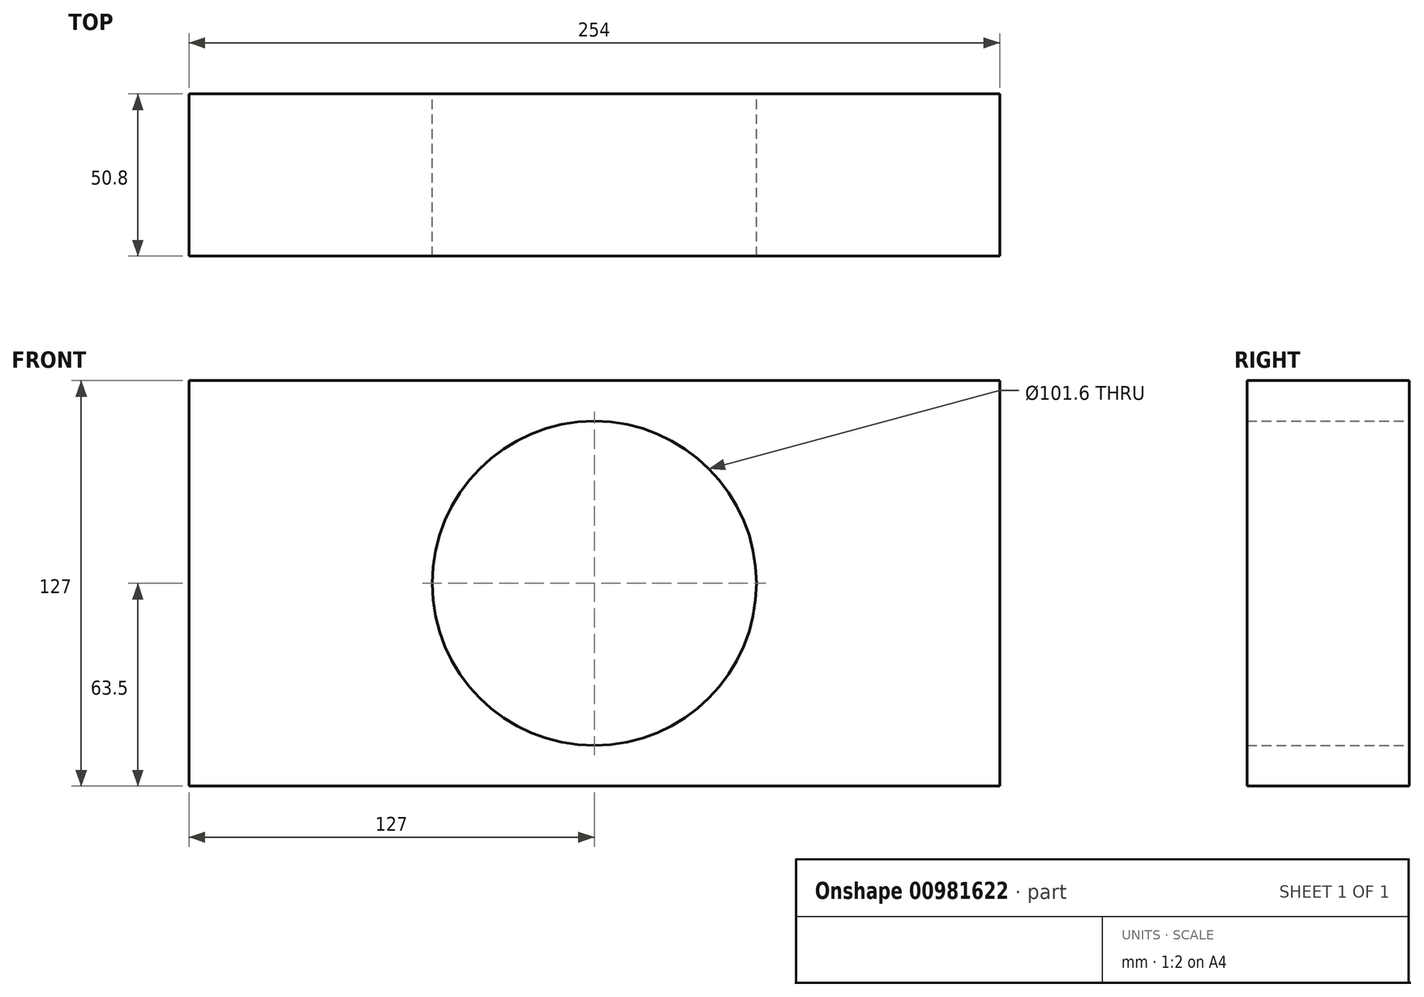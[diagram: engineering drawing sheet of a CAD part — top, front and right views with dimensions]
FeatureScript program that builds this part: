
annotation { "Feature Type Name" : "Feature", "Feature Type Description" : "" }
export const myFeature = defineFeature(function(context is Context, id is Id, definition is map)
    precondition{}
    {
        {
            var Q0;
            Q0=qCreatedBy(makeId("Front.planeOp"),FACE);
            var sketch = newSketch(context, id + "F0", { "sketchPlane" : qUnion([Q0])});
            skLineSegment(sketch, "E0.bottom", {"start": v(-127, -63.5) * mm, "end": v(127, -63.5) * mm});
            skLineSegment(sketch, "E0.top", {"start": v(-127, 63.5) * mm, "end": v(127, 63.5) * mm});
            skLineSegment(sketch, "E0.left", {"start": v(-127, -63.5) * mm, "end": v(-127, 63.5) * mm});
            skLineSegment(sketch, "E0.right", {"start": v(127, -63.5) * mm, "end": v(127, 63.5) * mm});
            skPoint(sketch, "E0.middle", {"position": v(0, 0) * mm});
            skCircle(sketch, "E1", {"center": v(0, 0) * mm, "radius": 50.8 * mm});
            skSolve(sketch);
        }
        {
            var Q0;
            Q0=makeQuery(id+"F0.imprint","IMPRINT",FACE,{"disambiguationData":[TD([[makeQuery(id+"F0.imprint","IMPRINT",EDGE,{"derivedFrom":sQuery(id+"F0.wireOp",EDGE,"E0.bottom")}),1.0]])]});
            var Q1;
            Q1 = qSketchRegion(id + "F2", true);
            extrude(context, id + "F1", {"entities" : qUnion([Q0, Q1]), "depth" : 50.8 * mm, "offsetDistance" : 25 * mm});
        }
        {
            var Q0;
            Q0=makeQuery(id+"F1.opExtrude","CAP_FACE",FACE,{"disambiguationData":[OSD([sQuery(id+"F0.wireOp",EDGE,"E0.bottom"),sQuery(id+"F0.wireOp",EDGE,"E0.top"),sQuery(id+"F0.wireOp",EDGE,"E0.left"),sQuery(id+"F0.wireOp",EDGE,"E0.right"),sQuery(id+"F0.wireOp",EDGE,"E1")])],"isStart":false});
            var sketch = newSketch(context, id + "F2", { "sketchPlane" : qUnion([Q0])});
            skLineSegment(sketch, "E2.bottom", {"start": v(-105.35, 63.5) * mm, "end": v(-79.95, 63.5) * mm});
            skLineSegment(sketch, "E2.top", {"start": v(-105.35, -63.5) * mm, "end": v(-79.95, -63.5) * mm});
            skLineSegment(sketch, "E2.left", {"start": v(-105.35, 63.5) * mm, "end": v(-105.35, -63.5) * mm});
            skLineSegment(sketch, "E2.right", {"start": v(-79.95, 63.5) * mm, "end": v(-79.95, -63.5) * mm});
            skLineSegment(sketch, "E3", {"start": v(-25.4, 63.5) * mm, "end": v(-25.4, -63.5) * mm});
            skLineSegment(sketch, "E4", {"start": v(-25.4, -63.5) * mm, "end": v(25.4, -63.5) * mm});
            skLineSegment(sketch, "E5", {"start": v(25.4, -63.5) * mm, "end": v(25.4, 63.5) * mm});
            skLineSegment(sketch, "E6", {"start": v(25.4, 63.5) * mm, "end": v(-25.4, 63.5) * mm});
            skPoint(sketch, "E7", {"position": v(0, 0) * mm});
            skLineSegment(sketch, "E8", {"start": v(0, 63.5) * mm, "end": v(0, -63.5) * mm, "construction": true});
            skSolve(sketch);
        }
    });
